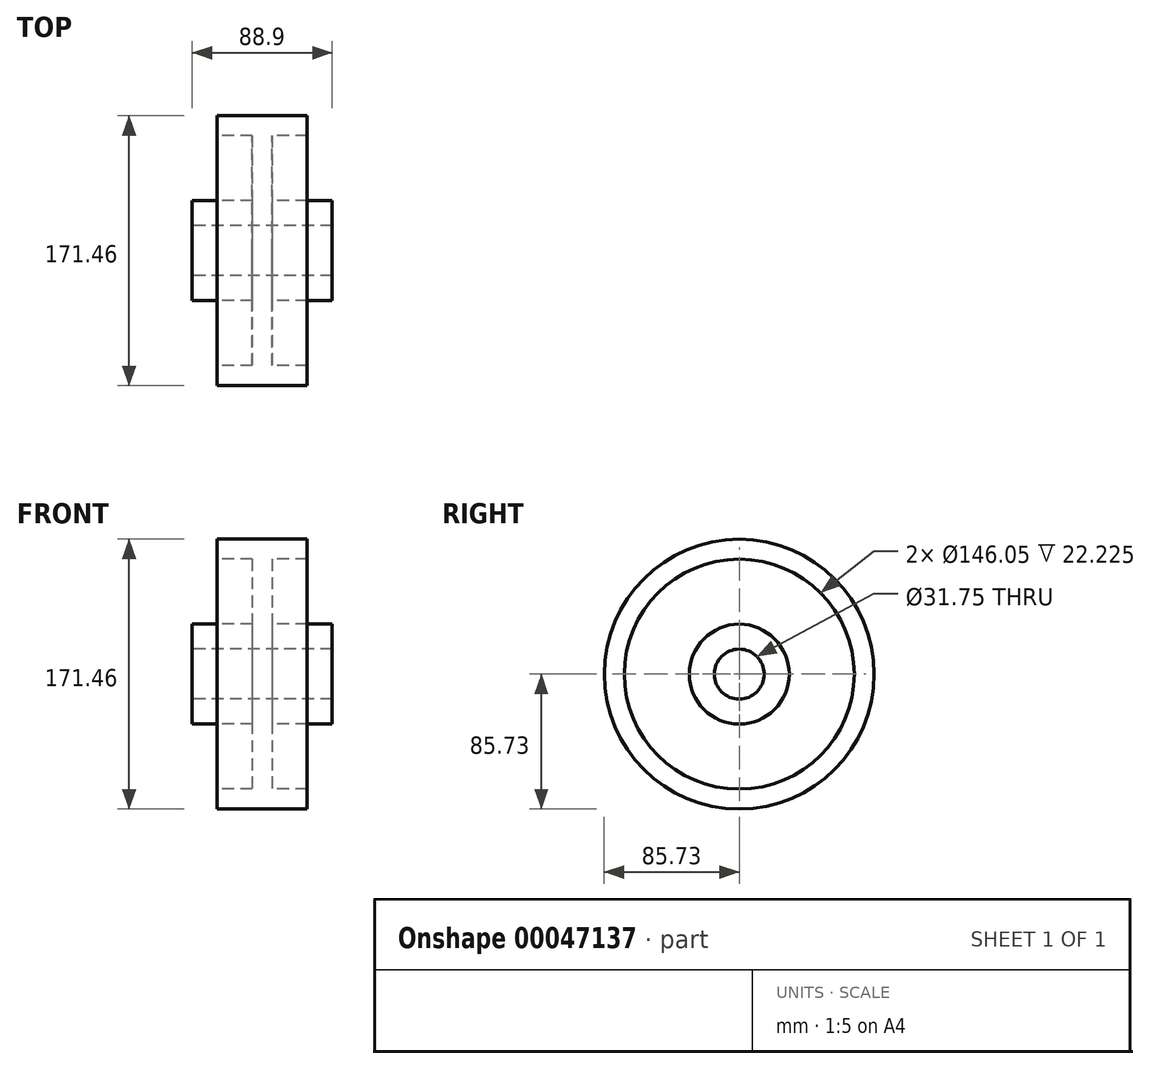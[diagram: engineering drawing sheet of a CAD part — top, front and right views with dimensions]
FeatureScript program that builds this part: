
annotation { "Feature Type Name" : "Feature", "Feature Type Description" : "" }
export const myFeature = defineFeature(function(context is Context, id is Id, definition is map)
    precondition{}
    {
        {
            var Q0;
            Q0=qCreatedBy(makeId("Front.planeOp"),FACE);
            var sketch = newSketch(context, id + "F0", { "sketchPlane" : qUnion([Q0])});
            skLineSegment(sketch, "E0", {"start": v(-332.56, 0) * mm, "end": v(331.75, 0) * mm, "construction": true});
            skLineSegment(sketch, "E1", {"start": v(0, 0) * mm, "end": v(0, 228.52) * mm, "construction": true});
            skLineSegment(sketch, "E2", {"start": v(-28.58, 85.73) * mm, "end": v(28.58, 85.73) * mm});
            skLineSegment(sketch, "E3", {"start": v(28.58, 85.73) * mm, "end": v(28.58, 73.03) * mm});
            skLineSegment(sketch, "E4", {"start": v(28.57, 73.03) * mm, "end": v(6.35, 73.03) * mm});
            skLineSegment(sketch, "E5", {"start": v(6.35, 73.03) * mm, "end": v(6.35, 31.75) * mm});
            skLineSegment(sketch, "E6", {"start": v(6.35, 31.75) * mm, "end": v(44.45, 31.75) * mm});
            skLineSegment(sketch, "E7", {"start": v(44.45, 31.75) * mm, "end": v(44.45, 15.88) * mm});
            skLineSegment(sketch, "E8", {"start": v(44.45, 15.88) * mm, "end": v(-44.45, 15.88) * mm});
            skLineSegment(sketch, "E9", {"start": v(-44.45, 15.88) * mm, "end": v(-44.45, 31.75) * mm});
            skLineSegment(sketch, "E10", {"start": v(-44.45, 31.75) * mm, "end": v(-6.35, 31.75) * mm});
            skLineSegment(sketch, "E11", {"start": v(-6.35, 31.75) * mm, "end": v(-6.35, 73.03) * mm});
            skLineSegment(sketch, "E12", {"start": v(-6.35, 73.03) * mm, "end": v(-28.58, 73.03) * mm});
            skLineSegment(sketch, "E13", {"start": v(-28.58, 73.03) * mm, "end": v(-28.58, 85.73) * mm});
            skSolve(sketch);
        }
        {
            var Q0;
            Q0 = qSketchRegion(id + "F0", true);
            var Q1;
            Q1=sQuery(id+"F0.wireOp",EDGE,"E0");
            revolve(context, id + "F1", {"entities" : qUnion([Q0]), "axis" : qUnion([Q1]), "revolveType" : RevolveType.FULL});
        }
    });
